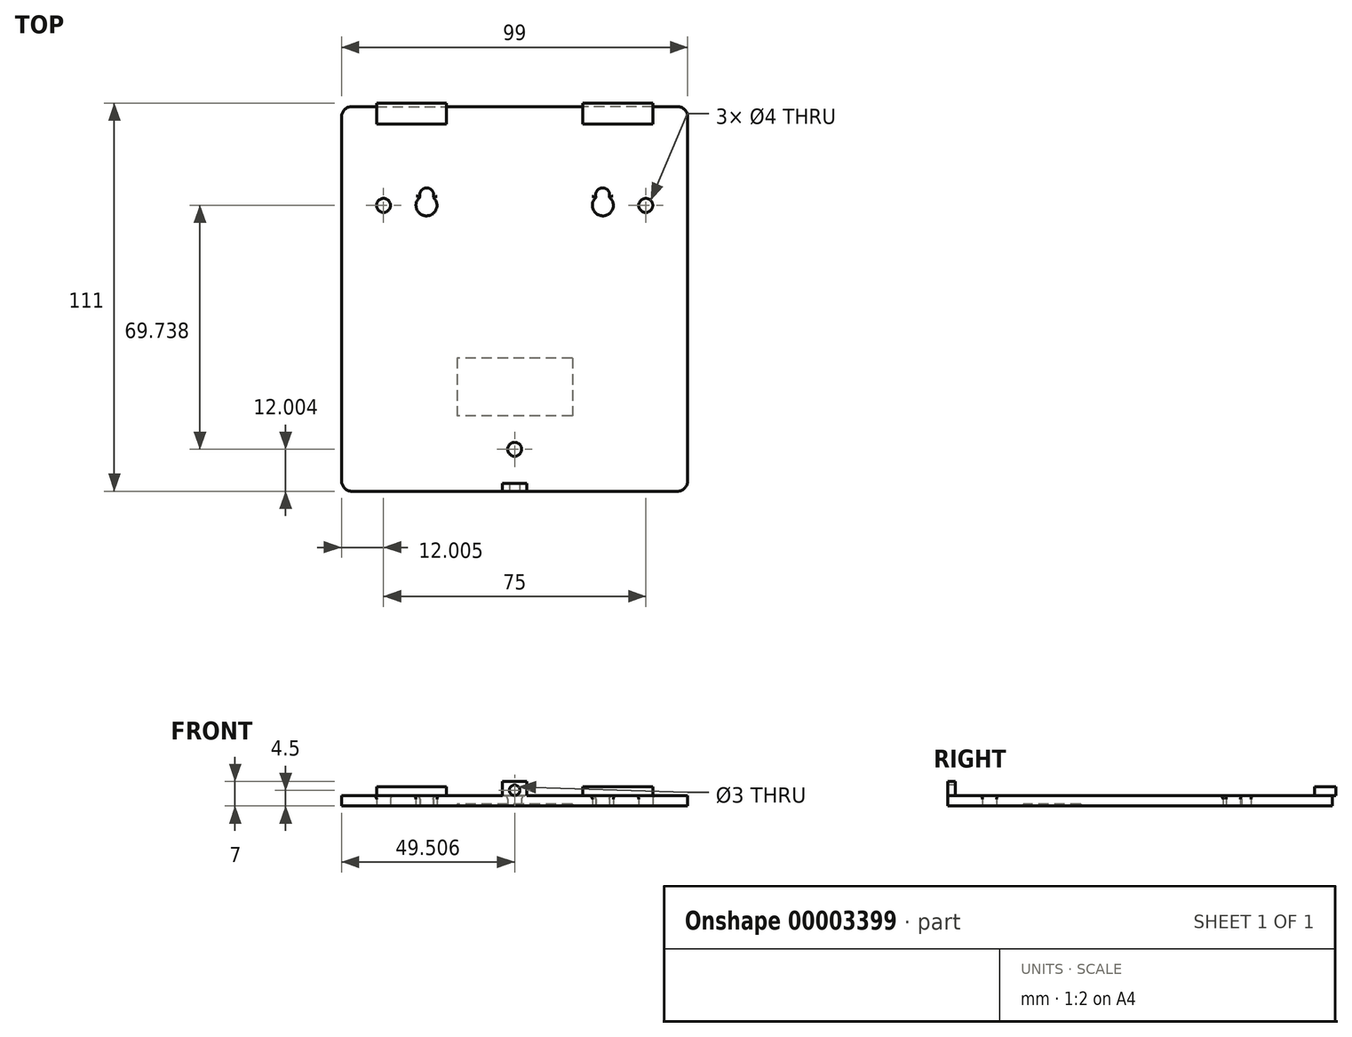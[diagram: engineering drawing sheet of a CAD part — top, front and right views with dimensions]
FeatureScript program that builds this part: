
annotation { "Feature Type Name" : "Feature", "Feature Type Description" : "" }
export const myFeature = defineFeature(function(context is Context, id is Id, definition is map)
    precondition{}
    {
        {
            var Q0;
            Q0=qCreatedBy(makeId("Top.planeOp"),FACE);
            var sketch = newSketch(context, id + "F0", { "sketchPlane" : qUnion([Q0])});
            skLineSegment(sketch, "E0.bottom", {"start": v(-82.84, 7) * mm, "end": v(16.16, 7) * mm});
            skLineSegment(sketch, "E0.top", {"start": v(-82.84, -103) * mm, "end": v(16.16, -103) * mm});
            skLineSegment(sketch, "E0.left", {"start": v(-82.84, 7) * mm, "end": v(-82.84, -103) * mm});
            skLineSegment(sketch, "E0.right", {"start": v(16.16, 7) * mm, "end": v(16.16, -103) * mm});
            skLineSegment(sketch, "E1", {"start": v(-33.34, -103) * mm, "end": v(-33.34, 7) * mm, "construction": true});
            skLineSegment(sketch, "E2", {"start": v(-82.84, -21.26) * mm, "end": v(16.16, -21.26) * mm, "construction": true});
            skCircle(sketch, "E3", {"center": v(-70.84, -21.26) * mm, "radius": 2 * mm});
            skCircle(sketch, "E4.0.MirrorC", {"center": v(4.16, -21.26) * mm, "radius": 2 * mm});
            skCircle(sketch, "E5", {"center": v(-33.34, -91) * mm, "radius": 2 * mm});
            skArc(sketch, "E6", {"start": v(-60.39, -18.88) * mm, "mid": v(-58.62, -24.26) * mm, "end": v(-56.62, -18.97) * mm});
            skArc(sketch, "E7", {"start": v(-56.62, -18.97) * mm, "mid": v(-58.44, -16.26) * mm, "end": v(-60.39, -18.88) * mm});
            skArc(sketch, "E8.0.MirrorCS", {"start": v(-10.05, -18.97) * mm, "mid": v(-8.23, -16.26) * mm, "end": v(-6.28, -18.88) * mm});
            skArc(sketch, "E8.1.MirrorCS", {"start": v(-6.28, -18.88) * mm, "mid": v(-8.05, -24.26) * mm, "end": v(-10.05, -18.97) * mm});
            skSolve(sketch);
        }
        {
            var Q0;
            Q0=makeQuery(id+"F0.imprint","IMPRINT",FACE,{"disambiguationData":[TD([[makeQuery(id+"F0.imprint","IMPRINT",EDGE,{"derivedFrom":sQuery(id+"F0.wireOp",EDGE,"E0.bottom")}),-1.0]])]});
            extrude(context, id + "F1", {"entities" : qUnion([Q0]), "depth" : 3 * mm});
        }
        {
            var Q0;
            Q0=makeQuery(id+"F1.opExtrude","CAP_EDGE",EDGE,{"disambiguationData":[OSD([sQuery(id+"F0.wireOp",EDGE,"E3")])],"isStart":false});
            var Q1;
            Q1=makeQuery(id+"F1.opExtrude","CAP_EDGE",EDGE,{"disambiguationData":[OSD([sQuery(id+"F0.wireOp",EDGE,"E4.0.MirrorC")])],"isStart":false});
            var Q2;
            Q2=makeQuery(id+"F1.opExtrude","CAP_EDGE",EDGE,{"disambiguationData":[OSD([sQuery(id+"F0.wireOp",EDGE,"E5")])],"isStart":false});
            var Q3;
            Q3=makeQuery(id+"F1.opExtrude","CAP_EDGE",EDGE,{"disambiguationData":[OSD([sQuery(id+"F0.wireOp",EDGE,"E7")])],"isStart":false});
            var Q4;
            Q4=makeQuery(id+"F1.opExtrude","CAP_EDGE",EDGE,{"disambiguationData":[OSD([sQuery(id+"F0.wireOp",EDGE,"E6")])],"isStart":false});
            var Q5;
            Q5=makeQuery(id+"F1.opExtrude","CAP_EDGE",EDGE,{"disambiguationData":[OSD([sQuery(id+"F0.wireOp",EDGE,"E8.0.MirrorCS")])],"isStart":false});
            var Q6;
            Q6=makeQuery(id+"F1.opExtrude","CAP_EDGE",EDGE,{"disambiguationData":[OSD([sQuery(id+"F0.wireOp",EDGE,"E8.1.MirrorCS")])],"isStart":false});
            fillet(context, id + "F2", {"entities" : qUnion([Q0, Q1, Q2, Q3, Q4, Q5, Q6]), "radius" : 1 * mm, "tangentPropagation" : true, "allowEdgeOverflow" : false});
        }
        {
            var Q0;
            Q0=makeQuery(id+"F1.opExtrude","SWEPT_EDGE",EDGE,{"disambiguationData":[OSD([sQuery(id+"F0.wireOp",EDGE,"E0.bottom"),sQuery(id+"F0.wireOp",EDGE,"E0.left")])]});
            var Q1;
            Q1=makeQuery(id+"F1.opExtrude","SWEPT_EDGE",EDGE,{"disambiguationData":[OSD([sQuery(id+"F0.wireOp",EDGE,"E0.bottom"),sQuery(id+"F0.wireOp",EDGE,"E0.right")])]});
            var Q2;
            Q2=makeQuery(id+"F1.opExtrude","SWEPT_EDGE",EDGE,{"disambiguationData":[OSD([sQuery(id+"F0.wireOp",EDGE,"E0.top"),sQuery(id+"F0.wireOp",EDGE,"E0.right")])]});
            var Q3;
            Q3=makeQuery(id+"F1.opExtrude","SWEPT_EDGE",EDGE,{"disambiguationData":[OSD([sQuery(id+"F0.wireOp",EDGE,"E0.top"),sQuery(id+"F0.wireOp",EDGE,"E0.left")])]});
            fillet(context, id + "F3", {"entities" : qUnion([Q0, Q1, Q2, Q3]), "radius" : 3 * mm, "tangentPropagation" : true, "allowEdgeOverflow" : false});
        }
        {
            var Q0;
            Q0=makeQuery(id+"F1.opExtrude","CAP_FACE",FACE,{"disambiguationData":[OSD([sQuery(id+"F0.wireOp",EDGE,"E0.bottom"),sQuery(id+"F0.wireOp",EDGE,"E0.top"),sQuery(id+"F0.wireOp",EDGE,"E0.left"),sQuery(id+"F0.wireOp",EDGE,"E0.right"),sQuery(id+"F0.wireOp",EDGE,"E3"),sQuery(id+"F0.wireOp",EDGE,"E4.0.MirrorC"),sQuery(id+"F0.wireOp",EDGE,"E5"),sQuery(id+"F0.wireOp",EDGE,"E6"),sQuery(id+"F0.wireOp",EDGE,"E7"),sQuery(id+"F0.wireOp",EDGE,"E8.0.MirrorCS"),sQuery(id+"F0.wireOp",EDGE,"E8.1.MirrorCS")])],"isStart":false});
            var sketch = newSketch(context, id + "F4", { "sketchPlane" : qUnion([Q0])});
            skLineSegment(sketch, "E9.bottom", {"start": v(-72.84, 7) * mm, "end": v(-52.84, 7) * mm});
            skLineSegment(sketch, "E9.top", {"start": v(-72.84, 2) * mm, "end": v(-52.84, 2) * mm});
            skLineSegment(sketch, "E9.left", {"start": v(-72.84, 7) * mm, "end": v(-72.84, 2) * mm});
            skLineSegment(sketch, "E9.right", {"start": v(-52.84, 7) * mm, "end": v(-52.84, 2) * mm});
            skLineSegment(sketch, "E10", {"start": v(-33.34, 7) * mm, "end": v(-33.34, -103) * mm, "construction": true});
            skLineSegment(sketch, "E11.0.MirrorCS", {"start": v(6.16, 2) * mm, "end": v(-13.84, 2) * mm});
            skLineSegment(sketch, "E12.0.MirrorCS", {"start": v(-13.84, 7) * mm, "end": v(-13.84, 2) * mm});
            skLineSegment(sketch, "E13.0.MirrorCS", {"start": v(6.16, 7) * mm, "end": v(-13.84, 7) * mm});
            skLineSegment(sketch, "E14.0.MirrorCS", {"start": v(6.16, 7) * mm, "end": v(6.16, 2) * mm});
            skSolve(sketch);
        }
        {
            var Q0;
            Q0=makeQuery(id+"F4.imprint","IMPRINT",FACE,{"disambiguationData":[TD([[makeQuery(id+"F4.imprint","IMPRINT",EDGE,{"derivedFrom":sQuery(id+"F4.wireOp",EDGE,"E9.bottom")}),-1.0]])]});
            var Q1;
            Q1=makeQuery(id+"F4.imprint","IMPRINT",FACE,{"disambiguationData":[TD([[makeQuery(id+"F4.imprint","IMPRINT",EDGE,{"derivedFrom":sQuery(id+"F4.wireOp",EDGE,"E11.0.MirrorCS")}),-1.0]])]});
            extrude(context, id + "F5", {"entities" : qUnion([Q0, Q1]), "operationType" : NewBodyOperationType.ADD, "depth" : 2.5 * mm});
        }
        {
            var Q0;
            Q0=makeQuery(id+"F5.boolean.opBoolean","MERGE",FACE,{"derivedFrom":[makeQuery(id+"F1.opExtrude","SWEPT_FACE",FACE,{"disambiguationData":[OSD([sQuery(id+"F0.wireOp",EDGE,"E0.bottom")])]}),makeQuery(id+"F5.opExtrude","SWEPT_FACE",FACE,{"disambiguationData":[OSD([sQuery(id+"F4.wireOp",EDGE,"E9.bottom")])]}),makeQuery(id+"F5.opExtrude","SWEPT_FACE",FACE,{"disambiguationData":[OSD([sQuery(id+"F4.wireOp",EDGE,"E13.0.MirrorCS")])]})]});
            var sketch = newSketch(context, id + "F6", { "sketchPlane" : qUnion([Q0])});
            skSolve(sketch);
        }
        {
            var Q0;
            {var subQ0=sQuery(id+"F0.wireOp",EDGE,"E0.bottom");Q0=makeQuery(id+"F6.imprint","IMPRINT",FACE,{"disambiguationData":[TD([[makeQuery(id+"F6.imprint","IMPRINT",EDGE,{"derivedFrom":makeQuery(id+"F1.opExtrude","CAP_EDGE",EDGE,{"disambiguationData":[OSD([subQ0])],"isStart":true})}),-1.0]])]});}
            var sketch = newSketch(context, id + "F7", { "sketchPlane" : qUnion([Q0])});
            skLineSegment(sketch, "E15.bottom", {"start": v(72.84, 3) * mm, "end": v(52.84, 3) * mm});
            skLineSegment(sketch, "E15.top", {"start": v(72.84, 5.5) * mm, "end": v(52.84, 5.5) * mm});
            skLineSegment(sketch, "E15.left", {"start": v(72.84, 3) * mm, "end": v(72.84, 5.5) * mm});
            skLineSegment(sketch, "E15.right", {"start": v(52.84, 3) * mm, "end": v(52.84, 5.5) * mm});
            skLineSegment(sketch, "E16", {"start": v(33.34, 2.99) * mm, "end": v(33.34, 0) * mm, "construction": true});
            skLineSegment(sketch, "E17.0.MirrorCS", {"start": v(-6.16, 5.5) * mm, "end": v(13.84, 5.5) * mm});
            skLineSegment(sketch, "E18.0.MirrorCS", {"start": v(-6.16, 3) * mm, "end": v(13.84, 3) * mm});
            skLineSegment(sketch, "E19.0.MirrorCS", {"start": v(13.84, 3) * mm, "end": v(13.84, 5.5) * mm});
            skLineSegment(sketch, "E20.0.MirrorCS", {"start": v(-6.16, 3) * mm, "end": v(-6.16, 5.5) * mm});
            skSolve(sketch);
        }
        {
            var Q0;
            Q0=makeQuery(id+"F7.imprint","IMPRINT",FACE,{"disambiguationData":[TD([[makeQuery(id+"F7.imprint","IMPRINT",EDGE,{"derivedFrom":sQuery(id+"F7.wireOp",EDGE,"E15.bottom")}),-1.0]])]});
            var Q1;
            {var subQ2=sQuery(id+"F7.wireOp",EDGE,"E20.0.MirrorCS");Q1=makeQuery(id+"F7.imprint","IMPRINT",FACE,{"disambiguationData":[TD([[makeQuery(id+"F7.imprint","IMPRINT",EDGE,{"derivedFrom":subQ2}),-1.0]])]});}
            extrude(context, id + "F8", {"entities" : qUnion([Q0, Q1]), "operationType" : NewBodyOperationType.ADD, "depth" : 1 * mm});
        }
        {
            var Q0;
            Q0=makeQuery(id+"F4.imprint","IMPRINT",FACE,{"disambiguationData":[TD([[makeQuery(id+"F4.imprint","IMPRINT",EDGE,{"derivedFrom":sQuery(id+"F4.wireOp",EDGE,"E9.top")}),-1.0]])]});
            var sketch = newSketch(context, id + "F9", { "sketchPlane" : qUnion([Q0])});
            skLineSegment(sketch, "E21.bottom", {"start": v(-36.83, -103) * mm, "end": v(-29.83, -103) * mm});
            skLineSegment(sketch, "E21.top", {"start": v(-36.83, -100.74) * mm, "end": v(-29.83, -100.74) * mm});
            skLineSegment(sketch, "E21.left", {"start": v(-36.83, -103) * mm, "end": v(-36.83, -100.74) * mm});
            skLineSegment(sketch, "E21.right", {"start": v(-29.83, -103) * mm, "end": v(-29.83, -100.74) * mm});
            skLineSegment(sketch, "E22", {"start": v(-33.33, -103) * mm, "end": v(-33.33, -100.74) * mm, "construction": true});
            skSolve(sketch);
        }
        {
            var Q0;
            Q0=makeQuery(id+"F9.imprint","IMPRINT",FACE,{"disambiguationData":[TD([[makeQuery(id+"F9.imprint","IMPRINT",EDGE,{"derivedFrom":sQuery(id+"F9.wireOp",EDGE,"E21.bottom")}),1.0]])]});
            extrude(context, id + "F10", {"entities" : qUnion([Q0]), "operationType" : NewBodyOperationType.ADD, "depth" : 4 * mm});
        }
        {
            var Q0;
            Q0=makeQuery(id+"F10.boolean.opBoolean","MERGE",FACE,{"derivedFrom":[makeQuery(id+"F1.opExtrude","SWEPT_FACE",FACE,{"disambiguationData":[OSD([sQuery(id+"F0.wireOp",EDGE,"E0.top")])]}),makeQuery(id+"F10.opExtrude","SWEPT_FACE",FACE,{"disambiguationData":[OSD([sQuery(id+"F9.wireOp",EDGE,"E21.bottom")])]})]});
            var sketch = newSketch(context, id + "F11", { "sketchPlane" : qUnion([Q0])});
            skCircle(sketch, "E23", {"center": v(-33.33, 4.5) * mm, "radius": 1.5 * mm});
            skSolve(sketch);
        }
        {
            var Q0;
            Q0=makeQuery(id+"F11.imprint","IMPRINT",FACE,{"disambiguationData":[TD([[makeQuery(id+"F11.imprint","IMPRINT",EDGE,{"derivedFrom":sQuery(id+"F11.wireOp",EDGE,"E23")}),1.0]])]});
            extrude(context, id + "F12", {"entities" : qUnion([Q0]), "operationType" : NewBodyOperationType.REMOVE, "endBound" : BoundingType.THROUGH_ALL, "oppositeDirection" : true, "depth" : 2.09 * mm});
        }
        {
            var Q0;
            Q0=makeQuery(id+"F0.imprint","IMPRINT",FACE,{"disambiguationData":[TD([[makeQuery(id+"F0.imprint","IMPRINT",EDGE,{"derivedFrom":sQuery(id+"F0.wireOp",EDGE,"E0.bottom")}),-1.0]])]});
            var sketch = newSketch(context, id + "F13", { "sketchPlane" : qUnion([Q0])});
            skLineSegment(sketch, "E24.bottom", {"start": v(-16.84, -64.9) * mm, "end": v(-49.84, -64.9) * mm});
            skLineSegment(sketch, "E24.top", {"start": v(-16.84, -81.4) * mm, "end": v(-49.84, -81.4) * mm});
            skLineSegment(sketch, "E24.left", {"start": v(-16.84, -64.9) * mm, "end": v(-16.84, -81.4) * mm});
            skLineSegment(sketch, "E24.right", {"start": v(-49.84, -64.9) * mm, "end": v(-49.84, -81.4) * mm});
            skSolve(sketch);
        }
        {
            var Q0;
            Q0=makeQuery(id+"F13.imprint","IMPRINT",FACE,{"disambiguationData":[TD([[makeQuery(id+"F13.imprint","IMPRINT",EDGE,{"derivedFrom":sQuery(id+"F13.wireOp",EDGE,"E24.bottom")}),1.0]])]});
            extrude(context, id + "F14", {"entities" : qUnion([Q0]), "operationType" : NewBodyOperationType.REMOVE, "depth" : 0.5 * mm});
        }
    });
